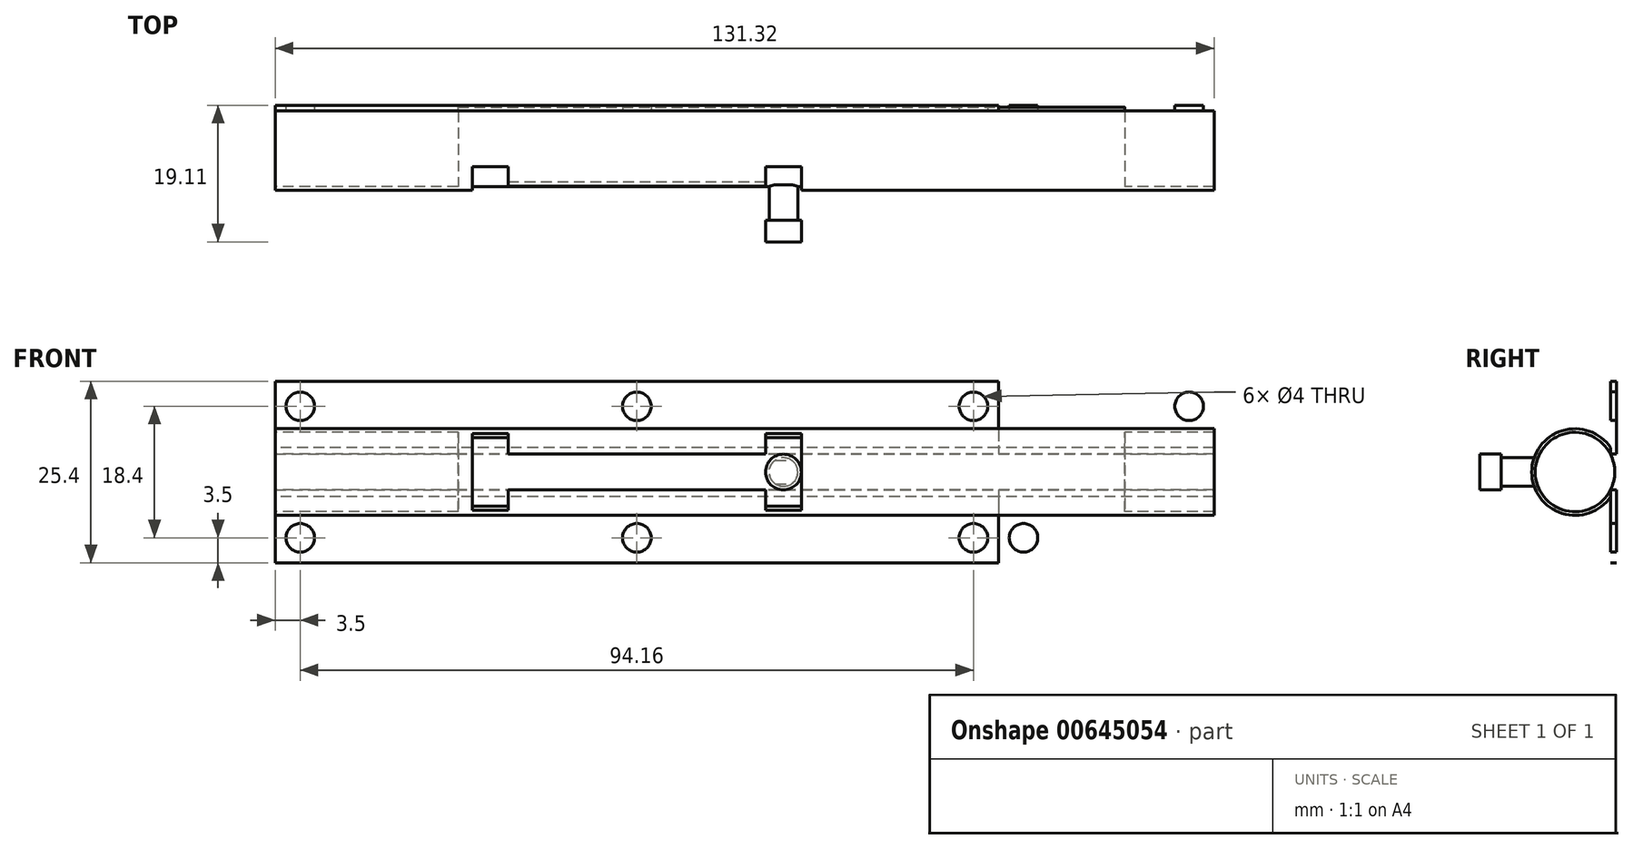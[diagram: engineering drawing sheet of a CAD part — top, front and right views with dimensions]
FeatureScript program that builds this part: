
annotation { "Feature Type Name" : "Feature", "Feature Type Description" : "" }
export const myFeature = defineFeature(function(context is Context, id is Id, definition is map)
    precondition{}
    {
        {
            var Q0;
            Q0=qCreatedBy(makeId("Front.planeOp"),FACE);
            var sketch = newSketch(context, id + "F0", { "sketchPlane" : qUnion([Q0])});
            skLineSegment(sketch, "E0.bottom", {"start": v(-50.58, 12.7) * mm, "end": v(50.58, 12.7) * mm});
            skLineSegment(sketch, "E0.top", {"start": v(-50.58, -12.7) * mm, "end": v(50.58, -12.7) * mm});
            skLineSegment(sketch, "E0.left", {"start": v(-50.58, 12.7) * mm, "end": v(-50.58, -12.7) * mm});
            skLineSegment(sketch, "E0.right", {"start": v(50.58, 12.7) * mm, "end": v(50.58, -12.7) * mm});
            skLineSegment(sketch, "E1", {"start": v(-50.58, 0) * mm, "end": v(0, 0) * mm, "construction": true});
            skLineSegment(sketch, "E2", {"start": v(0, 12.7) * mm, "end": v(0, 0) * mm, "construction": true});
            skLineSegment(sketch, "E3", {"start": v(0, 0) * mm, "end": v(0, -12.7) * mm, "construction": true});
            skLineSegment(sketch, "E4", {"start": v(-23, 2.5) * mm, "end": v(-23, -2.5) * mm});
            skLineSegment(sketch, "E5", {"start": v(-23, -2.5) * mm, "end": v(0, -2.5) * mm});
            skLineSegment(sketch, "E6", {"start": v(0, -2.5) * mm, "end": v(0, 2.5) * mm});
            skLineSegment(sketch, "E7", {"start": v(0, 2.5) * mm, "end": v(-23, 2.5) * mm});
            skLineSegment(sketch, "E8", {"start": v(0, 0) * mm, "end": v(-23, 0) * mm});
            skLineSegment(sketch, "E9.MirrorCS", {"start": v(-23, 7.5) * mm, "end": v(0, 7.5) * mm});
            skLineSegment(sketch, "E10.MirrorCS", {"start": v(-23, 2.5) * mm, "end": v(-23, 7.5) * mm});
            skLineSegment(sketch, "E11.MirrorCS", {"start": v(0, 2.5) * mm, "end": v(23, 2.5) * mm});
            skLineSegment(sketch, "E12.MirrorCS", {"start": v(23, 2.5) * mm, "end": v(23, -2.5) * mm});
            skLineSegment(sketch, "E13.MirrorCS", {"start": v(23, -2.5) * mm, "end": v(0, -2.5) * mm});
            skLineSegment(sketch, "E14", {"start": v(-23, 2.5) * mm, "end": v(-50.58, 2.5) * mm});
            skLineSegment(sketch, "E15", {"start": v(-23, -2.5) * mm, "end": v(-50.58, -2.5) * mm});
            skLineSegment(sketch, "E16", {"start": v(23, 2.5) * mm, "end": v(50.58, 2.5) * mm});
            skLineSegment(sketch, "E17", {"start": v(23, -2.5) * mm, "end": v(50.58, -2.5) * mm});
            skLineSegment(sketch, "E18", {"start": v(50.58, 12.7) * mm, "end": v(80.74, 12.7) * mm});
            skLineSegment(sketch, "E19", {"start": v(80.74, 12.7) * mm, "end": v(80.74, -12.7) * mm});
            skLineSegment(sketch, "E20", {"start": v(80.74, -12.7) * mm, "end": v(50.58, -12.7) * mm});
            skLineSegment(sketch, "E21", {"start": v(50.58, 2.5) * mm, "end": v(80.74, 2.5) * mm});
            skLineSegment(sketch, "E22", {"start": v(50.58, -2.5) * mm, "end": v(80.74, -2.5) * mm});
            skPoint(sketch, "E22.endSnap0", {"position": v(80.74, 0) * mm});
            skCircle(sketch, "E23", {"center": v(-47.08, 9.2) * mm, "radius": 2 * mm});
            skLineSegment(sketch, "E24", {"start": v(-47.08, 9.2) * mm, "end": v(-47.08, 12.7) * mm, "construction": true});
            skLineSegment(sketch, "E25", {"start": v(-47.08, 9.2) * mm, "end": v(-50.58, 9.2) * mm, "construction": true});
            skLineSegment(sketch, "E26", {"start": v(-47.08, 9.2) * mm, "end": v(0, 9.2) * mm, "construction": true});
            skCircle(sketch, "E27", {"center": v(0, 9.2) * mm, "radius": 2 * mm});
            skCircle(sketch, "E28.MirrorC", {"center": v(47.08, 9.2) * mm, "radius": 2 * mm});
            skCircle(sketch, "E29.MirrorC", {"center": v(-47.08, -9.2) * mm, "radius": 2 * mm});
            skCircle(sketch, "E30.MirrorC", {"center": v(0, -9.2) * mm, "radius": 2 * mm});
            skCircle(sketch, "E31.MirrorC", {"center": v(47.08, -9.2) * mm, "radius": 2 * mm});
            skLineSegment(sketch, "E32", {"start": v(50.58, 9.2) * mm, "end": v(54.08, 9.2) * mm, "construction": true});
            skLineSegment(sketch, "E33", {"start": v(54.08, 9.2) * mm, "end": v(54.08, 12.7) * mm, "construction": true});
            skCircle(sketch, "E34", {"center": v(54.08, 9.2) * mm, "radius": 2 * mm});
            skLineSegment(sketch, "E35", {"start": v(65.66, 12.7) * mm, "end": v(65.66, -12.7) * mm, "construction": true});
            skLineSegment(sketch, "E36", {"start": v(50.58, 0) * mm, "end": v(80.74, 0) * mm, "construction": true});
            skCircle(sketch, "E37.MirrorC", {"center": v(77.24, 9.2) * mm, "radius": 2 * mm});
            skCircle(sketch, "E38.MirrorC", {"center": v(54.08, -9.2) * mm, "radius": 2 * mm});
            skCircle(sketch, "E39.MirrorC", {"center": v(77.24, -9.2) * mm, "radius": 2 * mm});
            skSolve(sketch);
        }
        {
            var Q0;
            Q0=qCreatedBy(makeId("Right.planeOp"),FACE);
            var sketch = newSketch(context, id + "F1", { "sketchPlane" : qUnion([Q0])});
            skLineSegment(sketch, "E40", {"start": v(0, 12.7) * mm, "end": v(-17.85, 12.7) * mm});
            skLineSegment(sketch, "E41", {"start": v(0, 12.7) * mm, "end": v(0, -12.7) * mm, "construction": true});
            skLineSegment(sketch, "E42", {"start": v(0, 12.7) * mm, "end": v(12, 12.7) * mm, "construction": true});
            skLineSegment(sketch, "E43", {"start": v(12, 12.7) * mm, "end": v(12, -12.7) * mm, "construction": true});
            skLineSegment(sketch, "E44", {"start": v(12, -12.7) * mm, "end": v(0, -12.7) * mm, "construction": true});
            skLineSegment(sketch, "E45", {"start": v(12, 0) * mm, "end": v(-5, 0) * mm});
            skCircle(sketch, "E46", {"center": v(-5, 0) * mm, "radius": 5.56 * mm});
            skCircle(sketch, "E47", {"center": v(-5, 0) * mm, "radius": 6.06 * mm});
            skLineSegment(sketch, "E48", {"start": v(-10.56, 0) * mm, "end": v(-11.06, 0) * mm});
            skSolve(sketch);
        }
        {
            var Q0;
            Q0=makeQuery(id+"F0.imprint","IMPRINT",FACE,{"disambiguationData":[TD([[makeQuery(id+"F0.imprint","IMPRINT",EDGE,{"derivedFrom":sQuery(id+"F0.wireOp",EDGE,"E0.bottom")}),-1.0]])]});
            var Q1;
            {var subQ0=sQuery(id+"F0.wireOp",EDGE,"E5");Q1=makeQuery(id+"F0.imprint","IMPRINT",FACE,{"disambiguationData":[TD([[makeQuery(id+"F0.imprint","IMPRINT",EDGE,{"derivedFrom":subQ0}),1.0]])]});}
            var Q2;
            {var subQ0=sQuery(id+"F0.wireOp",EDGE,"E7");Q2=makeQuery(id+"F0.imprint","IMPRINT",FACE,{"disambiguationData":[TD([[makeQuery(id+"F0.imprint","IMPRINT",EDGE,{"derivedFrom":subQ0}),1.0]])]});}
            var Q3;
            {var subQ0=sQuery(id+"F0.wireOp",EDGE,"E11.MirrorCS");Q3=makeQuery(id+"F0.imprint","IMPRINT",FACE,{"disambiguationData":[TD([[makeQuery(id+"F0.imprint","IMPRINT",EDGE,{"derivedFrom":subQ0}),-1.0]])]});}
            var Q4;
            {var subQ2=sQuery(id+"F0.wireOp",EDGE,"E0.top");Q4=makeQuery(id+"F0.imprint","IMPRINT",FACE,{"disambiguationData":[TD([[makeQuery(id+"F0.imprint","IMPRINT",EDGE,{"derivedFrom":subQ2}),1.0]])]});}
            extrude(context, id + "F2", {"entities" : qUnion([Q0, Q1, Q2, Q3, Q4]), "oppositeDirection" : true, "depth" : .8 * mm, "offsetDistance" : 25 * mm});
        }
        {
            var Q0;
            {var subQ5=sQuery(id+"F1.wireOp",EDGE,"E48");Q0=makeQuery(id+"F1.imprint","IMPRINT",FACE,{"disambiguationData":[TD([[makeQuery(id+"F1.imprint","IMPRINT",EDGE,{"derivedFrom":subQ5}),-1.0]])]});}
            var Q1;
            {var subQ5=sQuery(id+"F1.wireOp",EDGE,"E48");Q1=makeQuery(id+"F1.imprint","IMPRINT",FACE,{"disambiguationData":[TD([[makeQuery(id+"F1.imprint","IMPRINT",EDGE,{"derivedFrom":subQ5}),1.0]])]});}
            var Q2;
            {var subQ0=sQuery(id+"F0.wireOp",EDGE,"E0.left");Q2=makeQuery(id+"F2.opExtrude","SWEPT_FACE",FACE,{"disambiguationData":[OSD([subQ0]),TDD([makeQuery(id+"F0.imprint","IMPRINT",EDGE,{"disambiguationData":[TD([[makeQuery(id+"F0.imprint","INTERSECT",VERTEX,{"derivedFrom":[sQuery(id+"F0.wireOp",EDGE,"E0.bottom"),subQ0]}),-1.0]])],"derivedFrom":subQ0})])]});}
            extrude(context, id + "F3", {"entities" : qUnion([Q0, Q1]), "operationType" : NewBodyOperationType.ADD, "depth" : 101.16 * mm, "endBoundEntityFace" : qUnion([Q2]), "offsetDistance" : 25 * mm, "symmetric" : true});
        }
        {
            var Q0;
            {var subQ0=sQuery(id+"F0.wireOp",EDGE,"E18");Q0=makeQuery(id+"F0.imprint","IMPRINT",FACE,{"disambiguationData":[TD([[makeQuery(id+"F0.imprint","IMPRINT",EDGE,{"derivedFrom":subQ0}),-1.0]])]});}
            var Q1;
            {var subQ0=sQuery(id+"F0.wireOp",EDGE,"E20");Q1=makeQuery(id+"F0.imprint","IMPRINT",FACE,{"disambiguationData":[TD([[makeQuery(id+"F0.imprint","IMPRINT",EDGE,{"derivedFrom":subQ0}),-1.0]])]});}
            extrude(context, id + "F4", {"entities" : qUnion([Q0, Q1]), "oppositeDirection" : true, "depth" : .8 * mm, "offsetDistance" : 25 * mm});
        }
        {
            var Q0;
            {var subQ0=sQuery(id+"F0.wireOp",EDGE,"E0.right");Q0=makeQuery(id+"F3.boolean.opBoolean","MERGE",FACE,{"derivedFrom":[makeQuery(id+"F2.opExtrude","SWEPT_FACE",FACE,{"disambiguationData":[OSD([subQ0]),TDD([makeQuery(id+"F0.imprint","IMPRINT",EDGE,{"disambiguationData":[TD([[makeQuery(id+"F0.imprint","INTERSECT",VERTEX,{"derivedFrom":[sQuery(id+"F0.wireOp",EDGE,"E0.bottom"),subQ0,sQuery(id+"F0.wireOp",EDGE,"E18")]}),-1.0]])],"derivedFrom":subQ0})])]}),makeQuery(id+"F2.opExtrude","SWEPT_FACE",FACE,{"disambiguationData":[OSD([subQ0]),TDD([makeQuery(id+"F0.imprint","IMPRINT",EDGE,{"disambiguationData":[TD([[makeQuery(id+"F0.imprint","INTERSECT",VERTEX,{"derivedFrom":[sQuery(id+"F0.wireOp",EDGE,"E0.top"),subQ0,sQuery(id+"F0.wireOp",EDGE,"E20")]}),1.0]])],"derivedFrom":subQ0})])]}),makeQuery(id+"F3.opExtrude","CAP_FACE",FACE,{"disambiguationData":[OSD([sQuery(id+"F1.wireOp",EDGE,"E46"),sQuery(id+"F1.wireOp",EDGE,"E47")])],"isStart":false})]});}
            extrude(context, id + "F5", {"entities" : qUnion([Q0]), "depth" : 30.16 * mm, "offsetDistance" : 25 * mm});
        }
        {
            var Q0;
            Q0=makeQuery(id+"F0.imprint","IMPRINT",FACE,{"disambiguationData":[TD([[makeQuery(id+"F0.imprint","IMPRINT",EDGE,{"derivedFrom":sQuery(id+"F0.wireOp",EDGE,"E34")}),1.0]])]});
            var Q1;
            Q1=makeQuery(id+"F0.imprint","IMPRINT",FACE,{"disambiguationData":[TD([[makeQuery(id+"F0.imprint","IMPRINT",EDGE,{"derivedFrom":sQuery(id+"F0.wireOp",EDGE,"E37.MirrorC")}),-1.0]])]});
            var Q2;
            Q2=makeQuery(id+"F0.imprint","IMPRINT",FACE,{"disambiguationData":[TD([[makeQuery(id+"F0.imprint","IMPRINT",EDGE,{"derivedFrom":sQuery(id+"F0.wireOp",EDGE,"E39.MirrorC")}),1.0]])]});
            var Q3;
            Q3=makeQuery(id+"F0.imprint","IMPRINT",FACE,{"disambiguationData":[TD([[makeQuery(id+"F0.imprint","IMPRINT",EDGE,{"derivedFrom":sQuery(id+"F0.wireOp",EDGE,"E38.MirrorC")}),-1.0]])]});
            extrude(context, id + "F6", {"entities" : qUnion([Q0, Q1, Q2, Q3]), "operationType" : NewBodyOperationType.REMOVE, "oppositeDirection" : true, "depth" : 25 * mm, "offsetDistance" : 25 * mm});
        }
        {
            var Q0;
            {var subQ0=sQuery(id+"F0.wireOp",EDGE,"E5");Q0=makeQuery(id+"F0.imprint","IMPRINT",FACE,{"disambiguationData":[TD([[makeQuery(id+"F0.imprint","IMPRINT",EDGE,{"derivedFrom":subQ0}),1.0]])]});}
            var Q1;
            {var subQ0=sQuery(id+"F0.wireOp",EDGE,"E7");Q1=makeQuery(id+"F0.imprint","IMPRINT",FACE,{"disambiguationData":[TD([[makeQuery(id+"F0.imprint","IMPRINT",EDGE,{"derivedFrom":subQ0}),1.0]])]});}
            var Q2;
            {var subQ0=sQuery(id+"F0.wireOp",EDGE,"E11.MirrorCS");Q2=makeQuery(id+"F0.imprint","IMPRINT",FACE,{"disambiguationData":[TD([[makeQuery(id+"F0.imprint","IMPRINT",EDGE,{"derivedFrom":subQ0}),-1.0]])]});}
            extrude(context, id + "F7", {"entities" : qUnion([Q0, Q1, Q2]), "operationType" : NewBodyOperationType.REMOVE, "depth" : 150 * mm, "offsetDistance" : 25 * mm, "symmetric" : true});
        }
        {
            var Q0;
            {var subQ3=sQuery(id+"F0.wireOp",EDGE,"E14");Q0=makeQuery(id+"F0.imprint","IMPRINT",FACE,{"disambiguationData":[TD([[makeQuery(id+"F0.imprint","IMPRINT",EDGE,{"derivedFrom":subQ3}),1.0]])]});}
            var Q1;
            Q1=makeQuery(id+"F0.imprint","IMPRINT",FACE,{"disambiguationData":[TD([[makeQuery(id+"F0.imprint","IMPRINT",EDGE,{"derivedFrom":sQuery(id+"F0.wireOp",EDGE,"E12.MirrorCS")}),1.0]])]});
            var Q2;
            {var subQ0=sQuery(id+"F0.wireOp",EDGE,"E21");Q2=makeQuery(id+"F0.imprint","IMPRINT",FACE,{"disambiguationData":[TD([[makeQuery(id+"F0.imprint","IMPRINT",EDGE,{"derivedFrom":subQ0}),-1.0]])]});}
            extrude(context, id + "F8", {"entities" : qUnion([Q0, Q1, Q2]), "operationType" : NewBodyOperationType.REMOVE, "depth" : 4 * mm, "offsetDistance" : 25 * mm, "symmetric" : true});
        }
        {
            var Q0;
            Q0=qCreatedBy(makeId("Front.planeOp"),FACE);
            cPlane(context, id + "F9", {"entities" : qUnion([Q0]), "cplaneType" : CPlaneType.OFFSET, "offset" : 12.8 * mm, "width" : 150 * mm, "height" : 150 * mm});
        }
        {
            var Q0;
            Q0=qCreatedBy(id+"F9.planeOp",FACE);
            var sketch = newSketch(context, id + "F10", { "sketchPlane" : qUnion([Q0])});
            skLineSegment(sketch, "E49", {"start": v(0, 7.16) * mm, "end": v(0, -6.5) * mm});
            skLineSegment(sketch, "E50.0", {"start": v(23, 2.5) * mm, "end": v(-23, 2.5) * mm});
            skLineSegment(sketch, "E51.0", {"start": v(-23, -2.5) * mm, "end": v(23, -2.5) * mm});
            skLineSegment(sketch, "E52.0", {"start": v(-23, 2.5) * mm, "end": v(-23, -2.5) * mm});
            skLineSegment(sketch, "E53.0", {"start": v(23, 2.5) * mm, "end": v(23, -2.5) * mm});
            skLineSegment(sketch, "E54", {"start": v(-23, 2.5) * mm, "end": v(-23, 7.5) * mm});
            skLineSegment(sketch, "E55", {"start": v(-23, 7.5) * mm, "end": v(-18, 7.5) * mm});
            skLineSegment(sketch, "E56", {"start": v(-18, 7.5) * mm, "end": v(-18, 2.5) * mm});
            skLineSegment(sketch, "E57", {"start": v(-23, -2.5) * mm, "end": v(-23, -7.5) * mm});
            skLineSegment(sketch, "E58", {"start": v(-23, -7.5) * mm, "end": v(-18, -7.5) * mm});
            skLineSegment(sketch, "E59", {"start": v(-18, -7.5) * mm, "end": v(-18, -2.5) * mm});
            skLineSegment(sketch, "E60.MirrorCS", {"start": v(23, 2.5) * mm, "end": v(23, 7.5) * mm});
            skLineSegment(sketch, "E61.MirrorCS", {"start": v(23, 7.5) * mm, "end": v(18, 7.5) * mm});
            skLineSegment(sketch, "E62.MirrorCS", {"start": v(18, 7.5) * mm, "end": v(18, 2.5) * mm});
            skLineSegment(sketch, "E63.MirrorCS", {"start": v(23, -2.5) * mm, "end": v(23, -7.5) * mm});
            skLineSegment(sketch, "E64.MirrorCS", {"start": v(23, -7.5) * mm, "end": v(18, -7.5) * mm});
            skLineSegment(sketch, "E65.MirrorCS", {"start": v(18, -7.5) * mm, "end": v(18, -2.5) * mm});
            skSolve(sketch);
        }
        {
            var Q0;
            {var subQ0=sQuery(id+"F10.wireOp",EDGE,"E54");Q0=makeQuery(id+"F10.imprint","IMPRINT",FACE,{"disambiguationData":[TD([[makeQuery(id+"F10.imprint","IMPRINT",EDGE,{"derivedFrom":subQ0}),-1.0]])]});}
            var Q1;
            {var subQ0=sQuery(id+"F10.wireOp",EDGE,"E57");Q1=makeQuery(id+"F10.imprint","IMPRINT",FACE,{"disambiguationData":[TD([[makeQuery(id+"F10.imprint","IMPRINT",EDGE,{"derivedFrom":subQ0}),1.0]])]});}
            var Q2;
            {var subQ0=sQuery(id+"F10.wireOp",EDGE,"E60.MirrorCS");Q2=makeQuery(id+"F10.imprint","IMPRINT",FACE,{"disambiguationData":[TD([[makeQuery(id+"F10.imprint","IMPRINT",EDGE,{"derivedFrom":subQ0}),1.0]])]});}
            var Q3;
            {var subQ0=sQuery(id+"F10.wireOp",EDGE,"E63.MirrorCS");Q3=makeQuery(id+"F10.imprint","IMPRINT",FACE,{"disambiguationData":[TD([[makeQuery(id+"F10.imprint","IMPRINT",EDGE,{"derivedFrom":subQ0}),-1.0]])]});}
            var Q4;
            {var subQ2=sQuery(id+"F0.wireOp",EDGE,"E0.left");var subQ3=sQuery(id+"F0.wireOp",EDGE,"E0.top");var subQ4=sQuery(id+"F0.wireOp",EDGE,"E15");var subQ5=sQuery(id+"F0.wireOp",EDGE,"E0.right");var subQ6=sQuery(id+"F0.wireOp",EDGE,"E17");Q4=makeQuery(id+"F3.boolean.opBoolean","SPLIT",FACE,{"disambiguationData":[TD([makeQuery(id+"F2.opExtrude","SWEPT_FACE",FACE,{"disambiguationData":[OSD([subQ3])]})])],"derivedFrom":makeQuery(id+"F2.opExtrude","CAP_FACE",FACE,{"disambiguationData":[OSD([sQuery(id+"F0.wireOp",EDGE,"E0.bottom"),subQ3,subQ2,subQ5,sQuery(id+"F0.wireOp",EDGE,"E4"),sQuery(id+"F0.wireOp",EDGE,"E12.MirrorCS"),sQuery(id+"F0.wireOp",EDGE,"E14"),subQ4,sQuery(id+"F0.wireOp",EDGE,"E16"),subQ6])],"isStart":true})});}
            extrude(context, id + "F11", {"entities" : qUnion([Q0, Q1, Q2, Q3]), "operationType" : NewBodyOperationType.REMOVE, "oppositeDirection" : true, "depth" : 5 * mm, "endBoundEntityFace" : qUnion([Q4]), "offsetDistance" : 25 * mm});
        }
        {
            var Q0;
            {var subQ0=sQuery(id+"F1.wireOp",EDGE,"E46");var subQ1=makeQuery(id+"F1.imprint","INTERSECT",VERTEX,{"derivedFrom":[subQ0,sQuery(id+"F1.wireOp",EDGE,"E48")]});Q0=makeQuery(id+"F1.imprint","IMPRINT",FACE,{"disambiguationData":[TD([[makeQuery(id+"F1.imprint","IMPRINT",EDGE,{"disambiguationData":[TD([[subQ1,1.0]])],"derivedFrom":subQ0}),1.0]])]});}
            extrude(context, id + "F12", {"entities" : qUnion([Q0]), "oppositeDirection" : true, "depth" : 25 * mm, "offsetDistance" : 25 * mm});
        }
        {
            var Q0;
            {var subQ0=sQuery(id+"F1.wireOp",EDGE,"E46");var subQ1=makeQuery(id+"F1.imprint","INTERSECT",VERTEX,{"derivedFrom":[subQ0,sQuery(id+"F1.wireOp",EDGE,"E48")]});Q0=makeQuery(id+"F1.imprint","IMPRINT",FACE,{"disambiguationData":[TD([[makeQuery(id+"F1.imprint","IMPRINT",EDGE,{"disambiguationData":[TD([[subQ1,1.0]])],"derivedFrom":subQ0}),1.0]])]});}
            extrude(context, id + "F13", {"entities" : qUnion([Q0]), "operationType" : NewBodyOperationType.ADD, "depth" : 50.8 * mm, "offsetDistance" : 25 * mm});
        }
        {
            var Q0;
            Q0=makeQuery(id+"F13.opExtrude","CAP_FACE",FACE,{"disambiguationData":[OSD([sQuery(id+"F1.wireOp",EDGE,"E46")])],"isStart":false});
            extrude(context, id + "F14", {"entities" : qUnion([Q0]), "operationType" : NewBodyOperationType.ADD, "depth" : 17.43 * mm, "offsetDistance" : 25 * mm});
        }
        {
            var Q0;
            Q0=qCreatedBy(id+"F9.planeOp",FACE);
            var sketch = newSketch(context, id + "F15", { "sketchPlane" : qUnion([Q0])});
            skLineSegment(sketch, "E66.0.0", {"start": v(0, 2.5) * mm, "end": v(0, -2.5) * mm, "construction": true});
            skLineSegment(sketch, "E66.0.1", {"start": v(0, -2.5) * mm, "end": v(18, -2.5) * mm, "construction": true});
            skLineSegment(sketch, "E66.0.2", {"start": v(18, -2.5) * mm, "end": v(23, -2.5) * mm, "construction": true});
            skLineSegment(sketch, "E66.0.3", {"start": v(23, -2.5) * mm, "end": v(23, 2.5) * mm, "construction": true});
            skLineSegment(sketch, "E66.0.4", {"start": v(23, 2.5) * mm, "end": v(18, 2.5) * mm, "construction": true});
            skLineSegment(sketch, "E66.0.5", {"start": v(18, 2.5) * mm, "end": v(0, 2.5) * mm, "construction": true});
            skLineSegment(sketch, "E67", {"start": v(18, 2.5) * mm, "end": v(18, -2.5) * mm, "construction": true});
            skLineSegment(sketch, "E68", {"start": v(18, 0) * mm, "end": v(23, 0) * mm, "construction": true});
            skLineSegment(sketch, "E69", {"start": v(20.5, -2.5) * mm, "end": v(20.5, 2.5) * mm, "construction": true});
            skCircle(sketch, "E70", {"center": v(20.5, 0) * mm, "radius": 2 * mm});
            skSolve(sketch);
        }
        {
            var Q0;
            Q0 = qSketchRegion(id + "F15", true);
            extrude(context, id + "F16", {"entities" : qUnion([Q0]), "operationType" : NewBodyOperationType.ADD, "depth" : 5 * mm, "offsetDistance" : 25 * mm, "symmetric" : true});
        }
        {
            var Q0;
            Q0=makeQuery(id+"F16.opExtrude","CAP_FACE",FACE,{"disambiguationData":[OSD([sQuery(id+"F15.wireOp",EDGE,"E70")])],"isStart":false});
            var sketch = newSketch(context, id + "F17", { "sketchPlane" : qUnion([Q0])});
            skCircle(sketch, "E71.0", {"center": v(20.5, 0) * mm, "radius": 2.34 * mm});
            skCircle(sketch, "E72", {"center": v(20.5, 0) * mm, "radius": 2.5 * mm});
            skSolve(sketch);
        }
        {
            var Q0;
            Q0=makeQuery(id+"F17.imprint","IMPRINT",FACE,{"disambiguationData":[TD([[makeQuery(id+"F17.imprint","IMPRINT",EDGE,{"derivedFrom":sQuery(id+"F17.wireOp",EDGE,"E71.0")}),-1.0]])]});
            var Q1;
            Q1=makeQuery(id+"F17.imprint","IMPRINT",FACE,{"disambiguationData":[TD([[makeQuery(id+"F17.imprint","IMPRINT",EDGE,{"derivedFrom":sQuery(id+"F17.wireOp",EDGE,"E71.0")}),1.0]])]});
            var Q2;
            Q2=makeQuery(id+"F17.imprint","IMPRINT",FACE,{"disambiguationData":[TD([[makeQuery(id+"F17.imprint","IMPRINT",EDGE,{"derivedFrom":makeQuery(id+"F16.opExtrude","CAP_EDGE",EDGE,{"disambiguationData":[OSD([sQuery(id+"F15.wireOp",EDGE,"E70")])],"isStart":false})}),1.0]])]});
            extrude(context, id + "F18", {"entities" : qUnion([Q0, Q1, Q2]), "operationType" : NewBodyOperationType.ADD, "depth" : 3 * mm, "offsetDistance" : 25 * mm});
        }
    });
